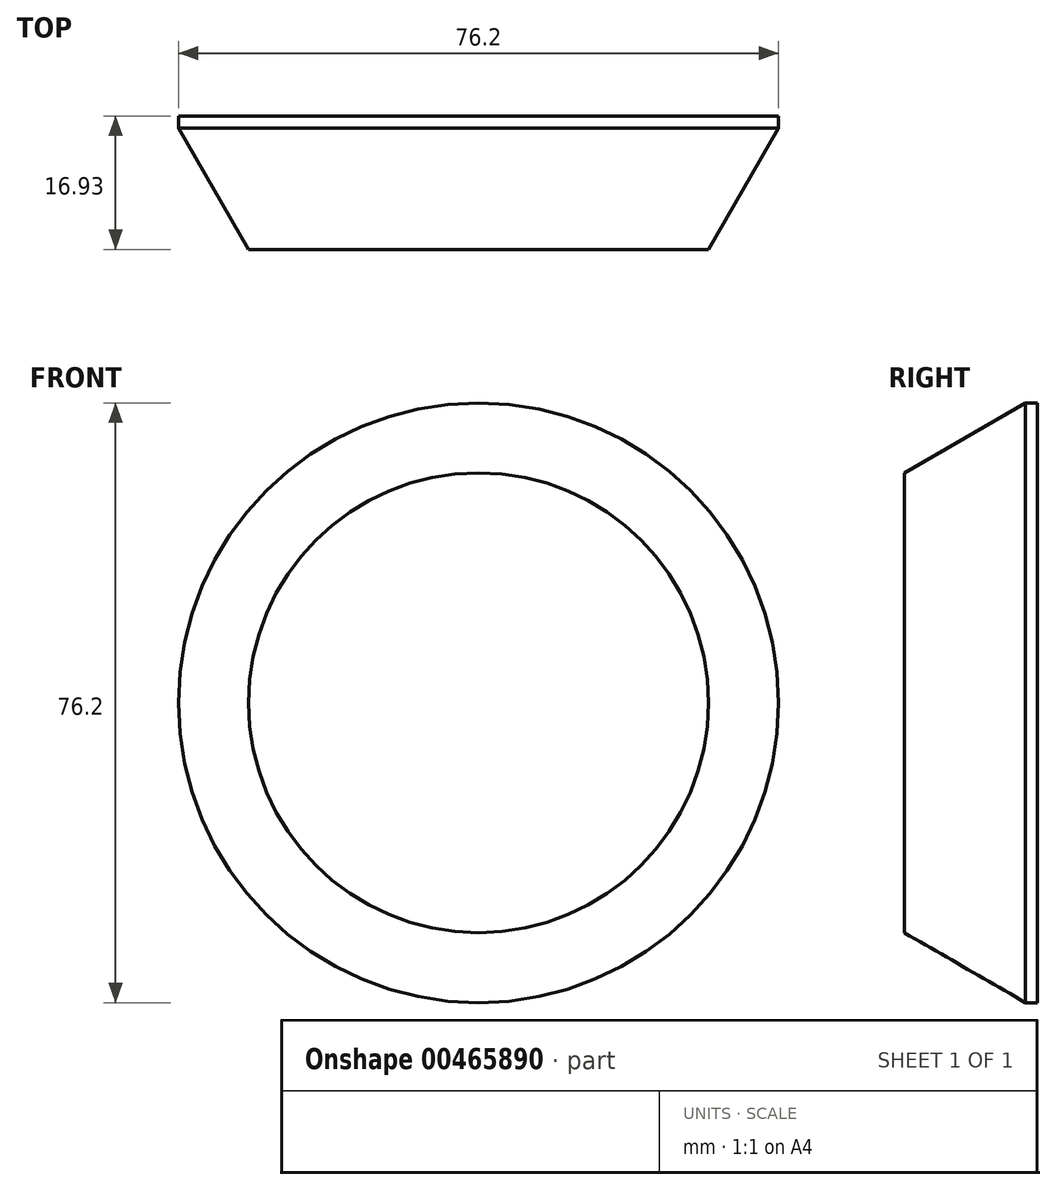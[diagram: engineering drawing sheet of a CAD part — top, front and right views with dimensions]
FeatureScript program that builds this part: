
annotation { "Feature Type Name" : "Feature", "Feature Type Description" : "" }
export const myFeature = defineFeature(function(context is Context, id is Id, definition is map)
    precondition{}
    {
        {
            var Q0;
            Q0=qCreatedBy(makeId("Front.planeOp"),FACE);
            var sketch = newSketch(context, id + "F0", { "sketchPlane" : qUnion([Q0])});
            skCircle(sketch, "E0", {"center": v(0, 0) * mm, "radius": 38.1 * mm});
            skSolve(sketch);
        }
        {
            var Q0;
            Q0=makeQuery(id+"F0.imprint","IMPRINT",FACE,{"disambiguationData":[TD([[makeQuery(id+"F0.imprint","IMPRINT",EDGE,{"derivedFrom":sQuery(id+"F0.wireOp",EDGE,"E0")}),1.0]])]});
            extrude(context, id + "F1", {"entities" : qUnion([Q0]), "depth" : 16.93 * mm, "offsetDistance" : 25.4 * mm});
        }
        {
            var Q0;
            Q0=makeQuery(id+"F1.opExtrude","CAP_EDGE",EDGE,{"disambiguationData":[OSD([sQuery(id+"F0.wireOp",EDGE,"E0")])],"isStart":false});
            chamfer(context, id + "F2", {"entities" : qUnion([Q0]), "chamferType" : ChamferType.OFFSET_ANGLE, "width" : 8.9 * mm, "oppositeDirection" : false, "angle" : 60 * degree, "tangentPropagation" : true});
        }
    });
